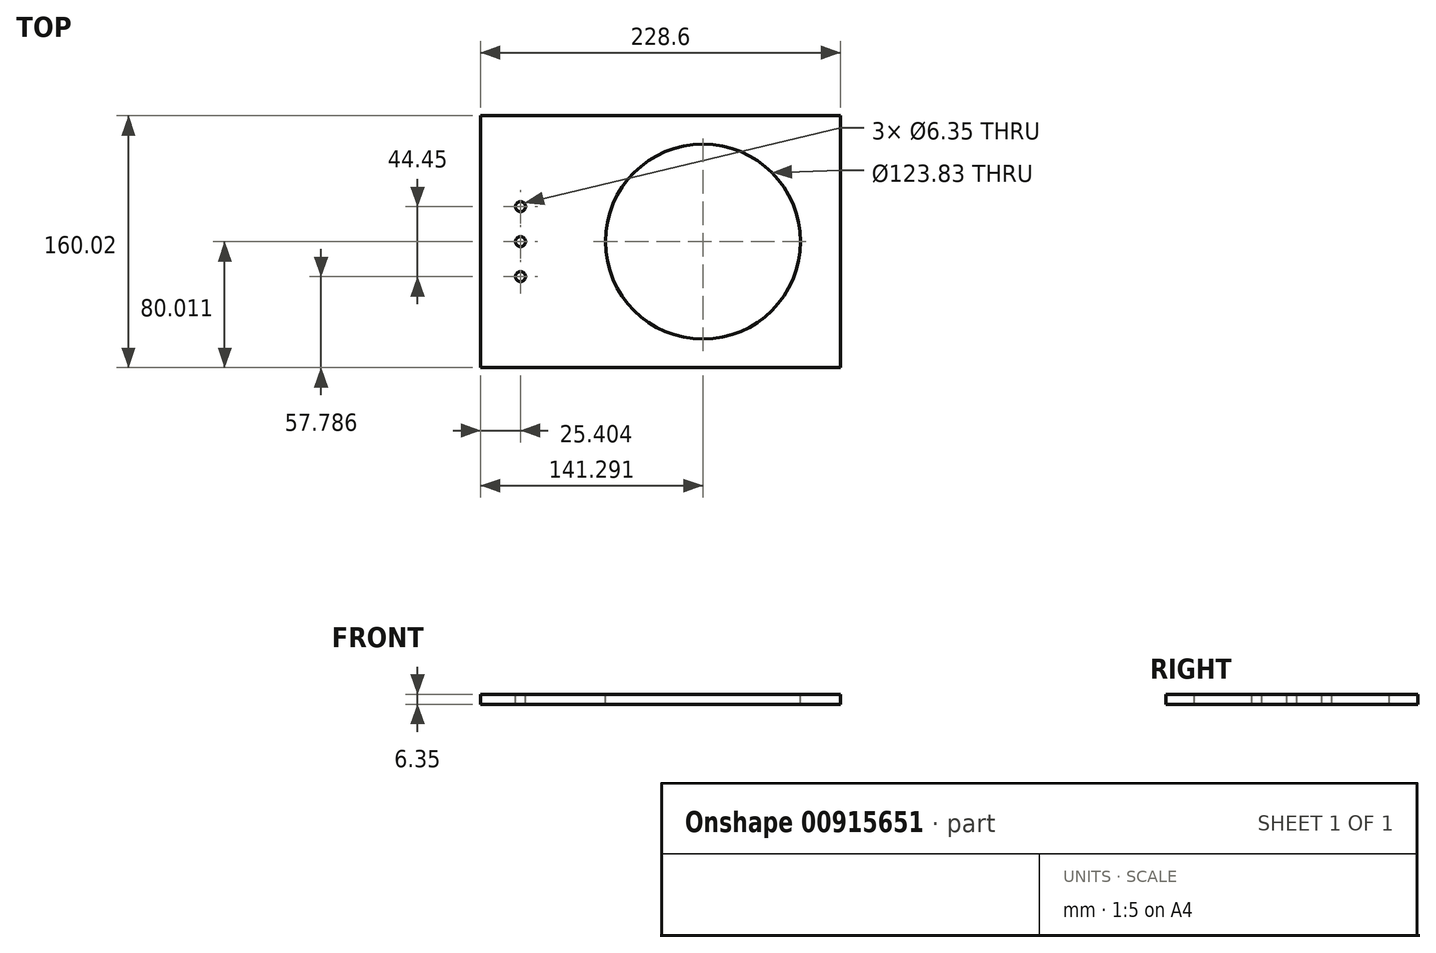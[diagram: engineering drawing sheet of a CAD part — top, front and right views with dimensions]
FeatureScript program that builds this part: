
annotation { "Feature Type Name" : "Feature", "Feature Type Description" : "" }
export const myFeature = defineFeature(function(context is Context, id is Id, definition is map)
    precondition{}
    {
        {
            var Q0;
            Q0=qCreatedBy(makeId("Top.planeOp"),FACE);
            var sketch = newSketch(context, id + "F0", { "sketchPlane" : qUnion([Q0])});
            skLineSegment(sketch, "E0.bottom", {"start": v(-113.52, 78.9) * mm, "end": v(115.08, 78.9) * mm});
            skLineSegment(sketch, "E0.top", {"start": v(-113.52, -81.12) * mm, "end": v(115.08, -81.12) * mm});
            skLineSegment(sketch, "E0.left", {"start": v(-113.52, 78.9) * mm, "end": v(-113.52, -81.12) * mm});
            skLineSegment(sketch, "E0.right", {"start": v(115.08, 78.9) * mm, "end": v(115.08, -81.12) * mm});
            skSolve(sketch);
        }
        {
            var Q0;
            Q0 = qSketchRegion(id + "F0", true);
            extrude(context, id + "F1", {"entities" : qUnion([Q0]), "depth" : 6.35 * mm, "offsetDistance" : 25.4 * mm});
        }
        {
            var Q0;
            Q0=makeQuery(id+"F1.opExtrude","CAP_FACE",FACE,{"disambiguationData":[OSD([sQuery(id+"F0.wireOp",EDGE,"E0.bottom"),sQuery(id+"F0.wireOp",EDGE,"E0.top"),sQuery(id+"F0.wireOp",EDGE,"E0.left"),sQuery(id+"F0.wireOp",EDGE,"E0.right")])],"isStart":false});
            var sketch = newSketch(context, id + "F2", { "sketchPlane" : qUnion([Q0])});
            skCircle(sketch, "E1", {"center": v(27.77, -1.1) * mm, "radius": 61.91 * mm});
            skSolve(sketch);
        }
        {
            var Q0;
            Q0=makeQuery(id+"F2.imprint","IMPRINT",FACE,{"disambiguationData":[TD([[makeQuery(id+"F2.imprint","IMPRINT",EDGE,{"derivedFrom":sQuery(id+"F2.wireOp",EDGE,"E1")}),1.0]])]});
            extrude(context, id + "F3", {"entities" : qUnion([Q0]), "operationType" : NewBodyOperationType.REMOVE, "oppositeDirection" : true, "depth" : 25.4 * mm, "offsetDistance" : 25.4 * mm});
        }
        {
            var Q0;
            Q0=makeQuery(id+"F1.opExtrude","CAP_FACE",FACE,{"disambiguationData":[OSD([sQuery(id+"F0.wireOp",EDGE,"E0.bottom"),sQuery(id+"F0.wireOp",EDGE,"E0.top"),sQuery(id+"F0.wireOp",EDGE,"E0.left"),sQuery(id+"F0.wireOp",EDGE,"E0.right")])],"isStart":false});
            var sketch = newSketch(context, id + "F4", { "sketchPlane" : qUnion([Q0])});
            skCircle(sketch, "E2", {"center": v(-88.12, -1.1) * mm, "radius": 3.18 * mm});
            skCircle(sketch, "E3", {"center": v(-88.12, -23.33) * mm, "radius": 3.18 * mm});
            skCircle(sketch, "E4", {"center": v(-88.12, 21.12) * mm, "radius": 3.18 * mm});
            skSolve(sketch);
        }
        {
            var Q0;
            Q0=makeQuery(id+"F4.imprint","IMPRINT",FACE,{"disambiguationData":[TD([[makeQuery(id+"F4.imprint","IMPRINT",EDGE,{"derivedFrom":sQuery(id+"F4.wireOp",EDGE,"E3")}),1.0]])]});
            var Q1;
            Q1=makeQuery(id+"F4.imprint","IMPRINT",FACE,{"disambiguationData":[TD([[makeQuery(id+"F4.imprint","IMPRINT",EDGE,{"derivedFrom":sQuery(id+"F4.wireOp",EDGE,"E2")}),1.0]])]});
            var Q2;
            Q2=makeQuery(id+"F4.imprint","IMPRINT",FACE,{"disambiguationData":[TD([[makeQuery(id+"F4.imprint","IMPRINT",EDGE,{"derivedFrom":sQuery(id+"F4.wireOp",EDGE,"E4")}),1.0]])]});
            extrude(context, id + "F5", {"entities" : qUnion([Q0, Q1, Q2]), "operationType" : NewBodyOperationType.REMOVE, "oppositeDirection" : true, "depth" : 25.4 * mm, "offsetDistance" : 25.4 * mm});
        }
    });
